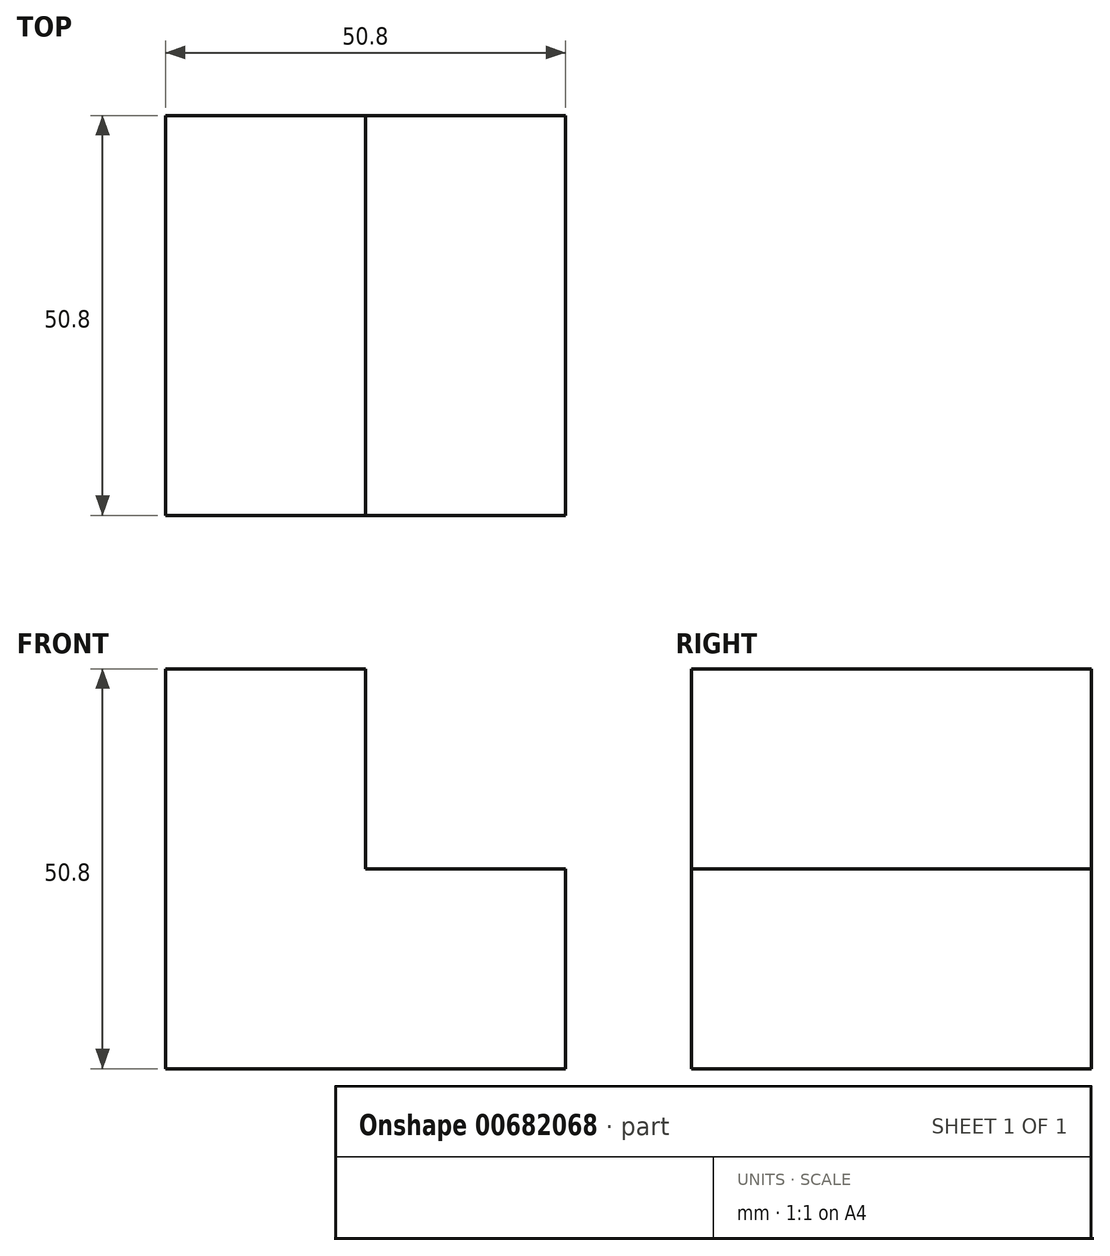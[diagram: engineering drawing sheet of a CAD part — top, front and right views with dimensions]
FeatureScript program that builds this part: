
annotation { "Feature Type Name" : "Feature", "Feature Type Description" : "" }
export const myFeature = defineFeature(function(context is Context, id is Id, definition is map)
    precondition{}
    {
        {
            var Q0;
            Q0=qCreatedBy(makeId("Front.planeOp"),FACE);
            var sketch = newSketch(context, id + "F0", { "sketchPlane" : qUnion([Q0])});
            skLineSegment(sketch, "E0", {"start": v(0, 0) * mm, "end": v(-50.8, 0) * mm});
            skLineSegment(sketch, "E1", {"start": v(-50.8, 0) * mm, "end": v(-50.8, 50.8) * mm});
            skLineSegment(sketch, "E2", {"start": v(-50.8, 50.8) * mm, "end": v(-25.4, 50.8) * mm});
            skLineSegment(sketch, "E3", {"start": v(-25.4, 50.8) * mm, "end": v(-25.4, 25.4) * mm});
            skLineSegment(sketch, "E4", {"start": v(-25.4, 25.4) * mm, "end": v(0, 25.4) * mm});
            skLineSegment(sketch, "E5", {"start": v(0, 25.4) * mm, "end": v(0, 0) * mm});
            skSolve(sketch);
        }
        {
            var Q0;
            Q0 = qSketchRegion(id + "F0", true);
            extrude(context, id + "F1", {"entities" : qUnion([Q0]), "depth" : 50.8 * mm, "offsetDistance" : 25.4 * mm});
        }
    });
